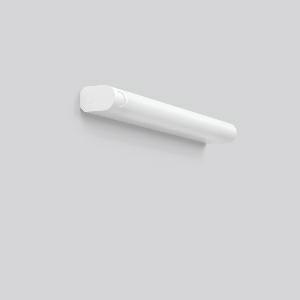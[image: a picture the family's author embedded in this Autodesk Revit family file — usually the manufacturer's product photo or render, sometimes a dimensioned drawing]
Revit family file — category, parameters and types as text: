
# Revit family: rt_44_451168_002_19_6c1b
name_source: partatom
category: Lighting Fixtures
units: mm (PartAtom-declared; Revit-internal decimal feet)

## family parameters
Cut with Voids When Loaded = No
Host = Face
Light Source = No
Part Type = Normal
Room Calculation Point = No
Round Connector Dimension = Use Diameter
Shared = No

## types (1)
- RT 44 (1 x LED Modul 830, 920 lm, 3000)
    Apparent Load = 10 VA
    CIE Flux Codes = 36 64 85 81 100
    Color Rendering = 80
    Color Temperature = 3000
    Default Elevation = 1800 mm
    Description = Series: RT 44
Linear luminaire, can be used as wall and mirror luminaire. Base: aluminium, powder-coated. End caps: plastic (polycarbonate), shock-resistant. Diffuser: plastic (polycarbonate), opal. Suitable for Ceiling mounting, Wall (surface). Can be installed horizontally and vertically. Very easy installation thanks to Plug+Play connection. Functional parameters of the IR movement sensor
installed on a ceiling at a height of max. 4 m or on a wall at a height of approx. 2.7 m. Range: 1-8 m in diameter, adjustable. Time control approx. 1 - 30 minutes, adjustable. Coverage: 360° horizontally and approx. 110° vertically. High type of protection: IP44 for use in wet areas. 
Colour: pure white (RAL 9010)
Length: 657 mm
Width: 55 mm
Height: 87 mm
Lamp: LED
Socket: without socket
Colour temperature: 3000K
Colour rendering index (CRI): 80
System power: 10 W
Rated luminous flux: 920 lm
Luminous efficiency: 92 lm/W
Control gear: Regulated power supply
Protection class: I
Type of protection: IP 44
    Height = 87 mm
    Lamp = 1 x LED Modul 830
    Lamp Light Flux = 920 lm
    Lamp count = 1
    Length = 657 mm
    Lifetime = 50000 h
    Luminous efficacy = 92 lm/W
    Manufacturer = RZB
    ModVariant = No
    Model = 451168.002.19
    Mounting Place = Ceiling, Wall
    Mounting Type = Surface mounted
    Number of Poles = 1
    OnlyDefault = Yes
    Power Factor = 1
    Product Name = RT 44
    Product group = Surface mounted ceiling and wall luminaires
    ProductGroupID = 305
    Protection Class = Protection class I
    Protection Degree = IP 44
    RLX_Detail_Level = 1
    RLX_Emergency_Light_Flux = 0 lm
    RLX_Emergency_Type = 0
    RLX_Emergency_Type_DB = No
    RlxData = <blob elided: 25497 chars, md5=2965712f>
    Socket = socket
    Standby Power = 0 W
    System Light Flux = 920 lm
    System Power = 10 W
    Type Comments = Product without accessories
    Type Image = 451054.752.19.jpg
    URL = http://relux.com
    VarID = ---
    Voltage = 230 V
    Voltage Range = 220-240 V
    Weight = 0.00 kg
    Width = 55 mm

## geometry (parser evidence)
native form markers: Blend x4, Sweep x15
no freeform markers — native parametric forms only
